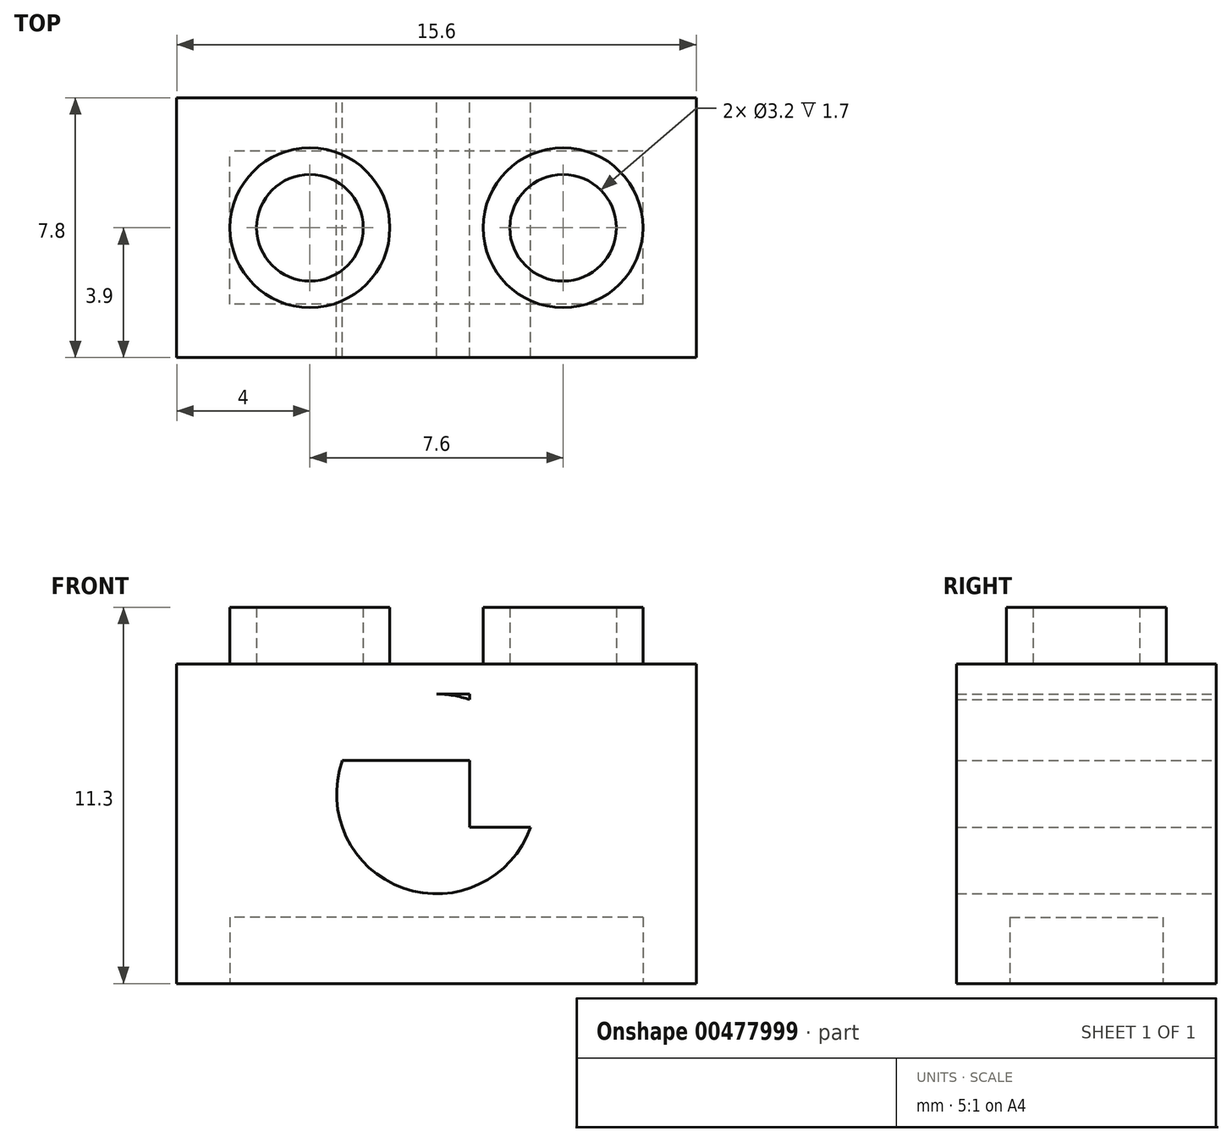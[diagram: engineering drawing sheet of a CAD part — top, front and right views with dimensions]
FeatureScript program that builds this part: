
annotation { "Feature Type Name" : "Feature", "Feature Type Description" : "" }
export const myFeature = defineFeature(function(context is Context, id is Id, definition is map)
    precondition{}
    {
        {
            var Q0;
            Q0=qCreatedBy(makeId("Front.planeOp"),FACE);
            var sketch = newSketch(context, id + "F0", { "sketchPlane" : qUnion([Q0])});
            skLineSegment(sketch, "E0", {"start": v(-0.25, 9.52) * mm, "end": v(-0.25, -0.08) * mm});
            skLineSegment(sketch, "E1", {"start": v(-0.25, -0.08) * mm, "end": v(15.35, -0.08) * mm});
            skLineSegment(sketch, "E2", {"start": v(15.35, -0.08) * mm, "end": v(15.35, 9.52) * mm});
            skLineSegment(sketch, "E3", {"start": v(-0.25, 9.52) * mm, "end": v(15.35, 9.52) * mm});
            skCircle(sketch, "E4", {"center": v(7.55, 5.62) * mm, "radius": 3 * mm});
            skPoint(sketch, "E4.centerSnap0", {"position": v(7.55, -0.08) * mm});
            skLineSegment(sketch, "E5.bottom", {"start": v(8.55, 8.62) * mm, "end": v(6.55, 8.62) * mm});
            skLineSegment(sketch, "E5.top", {"start": v(8.55, 2.62) * mm, "end": v(6.55, 2.62) * mm});
            skLineSegment(sketch, "E5.left", {"start": v(8.55, 8.62) * mm, "end": v(8.55, 2.62) * mm});
            skLineSegment(sketch, "E5.right", {"start": v(6.55, 8.62) * mm, "end": v(6.55, 2.62) * mm});
            skLineSegment(sketch, "E6.bottom", {"start": v(10.55, 6.62) * mm, "end": v(4.55, 6.62) * mm});
            skLineSegment(sketch, "E6.top", {"start": v(10.55, 4.62) * mm, "end": v(4.55, 4.62) * mm});
            skLineSegment(sketch, "E6.left", {"start": v(10.55, 6.62) * mm, "end": v(10.55, 4.62) * mm});
            skLineSegment(sketch, "E6.right", {"start": v(4.55, 6.62) * mm, "end": v(4.55, 4.62) * mm});
            skSolve(sketch);
        }
        {
            var Q0;
            {var subQ0=sQuery(id+"F0.wireOp",EDGE,"E6.left");var subQ1=sQuery(id+"F0.wireOp",EDGE,"E4");var subQ2=makeQuery(id+"F0.imprint","INTERSECT",VERTEX,{"derivedFrom":[subQ1,subQ0]});Q0=makeQuery(id+"F0.imprint","IMPRINT",FACE,{"disambiguationData":[TD([[makeQuery(id+"F0.imprint","IMPRINT",EDGE,{"disambiguationData":[TD([[subQ2,1.0]])],"derivedFrom":subQ1}),-1.0]])]});}
            var Q1;
            {var subQ0=sQuery(id+"F0.wireOp",EDGE,"E6.bottom");var subQ1=sQuery(id+"F0.wireOp",EDGE,"E4");var subQ2=makeQuery(id+"F0.imprint","INTERSECT",VERTEX,{"disambiguationData":[OD(0.0)],"derivedFrom":[subQ1,subQ0]});Q1=makeQuery(id+"F0.imprint","IMPRINT",FACE,{"disambiguationData":[TD([[makeQuery(id+"F0.imprint","IMPRINT",EDGE,{"disambiguationData":[TD([[subQ2,1.0]])],"derivedFrom":subQ1}),-1.0]])]});}
            var Q2;
            {var subQ0=sQuery(id+"F0.wireOp",EDGE,"E5.left");var subQ1=sQuery(id+"F0.wireOp",EDGE,"E4");var subQ2=makeQuery(id+"F0.imprint","INTERSECT",VERTEX,{"disambiguationData":[OD(0.0)],"derivedFrom":[subQ1,subQ0]});Q2=makeQuery(id+"F0.imprint","IMPRINT",FACE,{"disambiguationData":[TD([[makeQuery(id+"F0.imprint","IMPRINT",EDGE,{"disambiguationData":[TD([[subQ2,-1.0]])],"derivedFrom":subQ1}),-1.0]])]});}
            var Q3;
            {var subQ0=sQuery(id+"F0.wireOp",EDGE,"E5.bottom");var subQ1=sQuery(id+"F0.wireOp",EDGE,"E4");var subQ2=makeQuery(id+"F0.imprint","INTERSECT",VERTEX,{"derivedFrom":[subQ1,subQ0]});Q3=makeQuery(id+"F0.imprint","IMPRINT",FACE,{"disambiguationData":[TD([[makeQuery(id+"F0.imprint","IMPRINT",EDGE,{"disambiguationData":[TD([[subQ2,-1.0]])],"derivedFrom":subQ1}),-1.0]])]});}
            var Q4;
            {var subQ0=sQuery(id+"F0.wireOp",EDGE,"E6.bottom");var subQ1=sQuery(id+"F0.wireOp",EDGE,"E4");var subQ2=makeQuery(id+"F0.imprint","INTERSECT",VERTEX,{"disambiguationData":[OD(1.0)],"derivedFrom":[subQ1,subQ0]});Q4=makeQuery(id+"F0.imprint","IMPRINT",FACE,{"disambiguationData":[TD([[makeQuery(id+"F0.imprint","IMPRINT",EDGE,{"disambiguationData":[TD([[subQ2,-1.0]])],"derivedFrom":subQ1}),-1.0]])]});}
            var Q5;
            Q5=makeQuery(id+"F0.imprint","IMPRINT",FACE,{"disambiguationData":[TD([[makeQuery(id+"F0.imprint","IMPRINT",EDGE,{"derivedFrom":sQuery(id+"F0.wireOp",EDGE,"E0")}),1.0]])]});
            var Q6;
            {var subQ0=sQuery(id+"F0.wireOp",EDGE,"E6.right");var subQ1=sQuery(id+"F0.wireOp",EDGE,"E4");var subQ2=makeQuery(id+"F0.imprint","INTERSECT",VERTEX,{"derivedFrom":[subQ1,subQ0]});Q6=makeQuery(id+"F0.imprint","IMPRINT",FACE,{"disambiguationData":[TD([[makeQuery(id+"F0.imprint","IMPRINT",EDGE,{"disambiguationData":[TD([[subQ2,-1.0]])],"derivedFrom":subQ1}),-1.0]])]});}
            var Q7;
            {var subQ0=sQuery(id+"F0.wireOp",EDGE,"E5.right");var subQ1=sQuery(id+"F0.wireOp",EDGE,"E4");var subQ2=makeQuery(id+"F0.imprint","INTERSECT",VERTEX,{"disambiguationData":[OD(1.0)],"derivedFrom":[subQ1,subQ0]});Q7=makeQuery(id+"F0.imprint","IMPRINT",FACE,{"disambiguationData":[TD([[makeQuery(id+"F0.imprint","IMPRINT",EDGE,{"disambiguationData":[TD([[subQ2,-1.0]])],"derivedFrom":subQ1}),-1.0]])]});}
            var Q8;
            {var subQ0=sQuery(id+"F0.wireOp",EDGE,"E5.top");var subQ1=sQuery(id+"F0.wireOp",EDGE,"E4");var subQ2=makeQuery(id+"F0.imprint","INTERSECT",VERTEX,{"derivedFrom":[subQ1,subQ0]});Q8=makeQuery(id+"F0.imprint","IMPRINT",FACE,{"disambiguationData":[TD([[makeQuery(id+"F0.imprint","IMPRINT",EDGE,{"disambiguationData":[TD([[subQ2,-1.0]])],"derivedFrom":subQ1}),-1.0]])]});}
            var Q9;
            {var subQ0=sQuery(id+"F0.wireOp",EDGE,"E5.left");var subQ1=sQuery(id+"F0.wireOp",EDGE,"E4");var subQ2=makeQuery(id+"F0.imprint","INTERSECT",VERTEX,{"disambiguationData":[OD(1.0)],"derivedFrom":[subQ1,subQ0]});Q9=makeQuery(id+"F0.imprint","IMPRINT",FACE,{"disambiguationData":[TD([[makeQuery(id+"F0.imprint","IMPRINT",EDGE,{"disambiguationData":[TD([[subQ2,-1.0]])],"derivedFrom":subQ1}),1.0]])]});}
            var Q10;
            {var subQ0=sQuery(id+"F0.wireOp",EDGE,"E6.bottom");var subQ1=sQuery(id+"F0.wireOp",EDGE,"E4");var subQ2=makeQuery(id+"F0.imprint","INTERSECT",VERTEX,{"disambiguationData":[OD(0.0)],"derivedFrom":[subQ1,subQ0]});Q10=makeQuery(id+"F0.imprint","IMPRINT",FACE,{"disambiguationData":[TD([[makeQuery(id+"F0.imprint","IMPRINT",EDGE,{"disambiguationData":[TD([[subQ2,-1.0]])],"derivedFrom":subQ1}),1.0]])]});}
            var Q11;
            {var subQ0=sQuery(id+"F0.wireOp",EDGE,"E5.right");var subQ1=sQuery(id+"F0.wireOp",EDGE,"E4");var subQ2=makeQuery(id+"F0.imprint","INTERSECT",VERTEX,{"disambiguationData":[OD(0.0)],"derivedFrom":[subQ1,subQ0]});Q11=makeQuery(id+"F0.imprint","IMPRINT",FACE,{"disambiguationData":[TD([[makeQuery(id+"F0.imprint","IMPRINT",EDGE,{"disambiguationData":[TD([[subQ2,-1.0]])],"derivedFrom":subQ1}),1.0]])]});}
            var Q12;
            {var subQ0=sQuery(id+"F0.wireOp",EDGE,"E6.top");var subQ1=sQuery(id+"F0.wireOp",EDGE,"E4");var subQ2=makeQuery(id+"F0.imprint","INTERSECT",VERTEX,{"disambiguationData":[OD(0.0)],"derivedFrom":[subQ1,subQ0]});Q12=makeQuery(id+"F0.imprint","IMPRINT",FACE,{"disambiguationData":[TD([[makeQuery(id+"F0.imprint","IMPRINT",EDGE,{"disambiguationData":[TD([[subQ2,-1.0]])],"derivedFrom":subQ1}),1.0]])]});}
            var Q13;
            Q13 = qSketchRegion(id + "F2", true);
            extrude(context, id + "F1", {"entities" : qUnion([Q0, Q1, Q2, Q3, Q4, Q5, Q6, Q7, Q8, Q9, Q10, Q11, Q12, Q13]), "depth" : 7.8 * mm});
        }
        {
            var Q0;
            Q0=makeQuery(id+"F1.opExtrude","SWEPT_FACE",FACE,{"disambiguationData":[OSD([sQuery(id+"F0.wireOp",EDGE,"E3")])]});
            var sketch = newSketch(context, id + "F2", { "sketchPlane" : qUnion([Q0])});
            skCircle(sketch, "E7", {"center": v(3.75, -3.9) * mm, "radius": 2.4 * mm});
            skPoint(sketch, "E7.centerSnap0", {"position": v(-0.25, -3.9) * mm});
            skCircle(sketch, "E8", {"center": v(11.35, -3.9) * mm, "radius": 2.4 * mm});
            skPoint(sketch, "E8.centerSnap0", {"position": v(15.35, -3.9) * mm});
            skLineSegment(sketch, "E9", {"start": v(7.55, 0) * mm, "end": v(7.55, -7.8) * mm});
            skCircle(sketch, "E10", {"center": v(3.75, -3.9) * mm, "radius": 1.6 * mm});
            skCircle(sketch, "E11", {"center": v(11.35, -3.9) * mm, "radius": 1.6 * mm});
            skSolve(sketch);
        }
        {
            var Q0;
            Q0=makeQuery(id+"F2.imprint","IMPRINT",FACE,{"disambiguationData":[TD([[makeQuery(id+"F2.imprint","IMPRINT",EDGE,{"derivedFrom":sQuery(id+"F2.wireOp",EDGE,"E7")}),1.0]])]});
            var Q1;
            Q1=makeQuery(id+"F2.imprint","IMPRINT",FACE,{"disambiguationData":[TD([[makeQuery(id+"F2.imprint","IMPRINT",EDGE,{"derivedFrom":sQuery(id+"F2.wireOp",EDGE,"E8")}),1.0]])]});
            extrude(context, id + "F3", {"entities" : qUnion([Q0, Q1]), "operationType" : NewBodyOperationType.ADD, "depth" : 1.7 * mm});
        }
        {
            var Q0;
            Q0=makeQuery(id+"F1.opExtrude","SWEPT_FACE",FACE,{"disambiguationData":[OSD([sQuery(id+"F0.wireOp",EDGE,"E1")])]});
            var sketch = newSketch(context, id + "F4", { "sketchPlane" : qUnion([Q0])});
            skLineSegment(sketch, "E12", {"start": v(-0.25, 3.9) * mm, "end": v(1.35, 3.9) * mm});
            skLineSegment(sketch, "E13", {"start": v(7.55, 7.8) * mm, "end": v(7.55, 6.2) * mm});
            skLineSegment(sketch, "E14.bottom", {"start": v(13.75, 6.2) * mm, "end": v(1.35, 6.2) * mm});
            skLineSegment(sketch, "E14.top", {"start": v(13.75, 1.6) * mm, "end": v(1.35, 1.6) * mm});
            skLineSegment(sketch, "E14.left", {"start": v(13.75, 6.2) * mm, "end": v(13.75, 1.6) * mm});
            skLineSegment(sketch, "E14.right", {"start": v(1.35, 6.2) * mm, "end": v(1.35, 1.6) * mm});
            skLineSegment(sketch, "E15.trimOffspring", {"start": v(13.75, 3.9) * mm, "end": v(15.35, 3.9) * mm});
            skLineSegment(sketch, "E16.trimOffspring", {"start": v(7.55, 1.6) * mm, "end": v(7.55, 0) * mm});
            skSolve(sketch);
        }
        {
            var Q0;
            {var subQ6=sQuery(id+"F4.wireOp",EDGE,"E14.bottom");var subQ7=makeQuery(id+"F4.imprint","INTERSECT",VERTEX,{"derivedFrom":[sQuery(id+"F4.wireOp",EDGE,"E13"),subQ6]});Q0=makeQuery(id+"F4.imprint","IMPRINT",FACE,{"disambiguationData":[TD([[makeQuery(id+"F4.imprint","IMPRINT",EDGE,{"disambiguationData":[TD([[subQ7,1.0]])],"derivedFrom":subQ6}),1.0]])]});}
            extrude(context, id + "F5", {"entities" : qUnion([Q0]), "operationType" : NewBodyOperationType.REMOVE, "oppositeDirection" : true, "depth" : 2 * mm});
        }
    });
